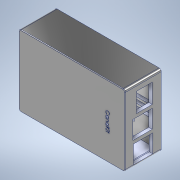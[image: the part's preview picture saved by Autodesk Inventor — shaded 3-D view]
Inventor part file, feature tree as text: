
AUTODESK INVENTOR PART (.ipt)
format: ipt  version: 2022.1 (Build 261234000, 234)  size: 506,368 bytes
history: mixed  units: in
note: dims shown in document units (in); Inventor stores cm internally (conversion verified against a paired STEP export)
features: fillet x1, imported_body x1
ambient origin geometry x8: Origin, YZ Plane, XZ Plane, XY Plane, X Axis, Y Axis, Z Axis, Center Point
bodies: Solid1 (imported_parasolid)
feature tree (2):
  fillet  "Fillet2"  [1 undecoded]
  imported_body  NMx_Import_Brep_tag  [imported B-rep: ~37 faces, bbox_mm=[92.0, 63.0, 31.5]]
note: 1 required parameter value undecoded (feature->parameter linkage not recoverable at this tier; creation-order binding heuristic only, values carry confidence <= 0.55)
